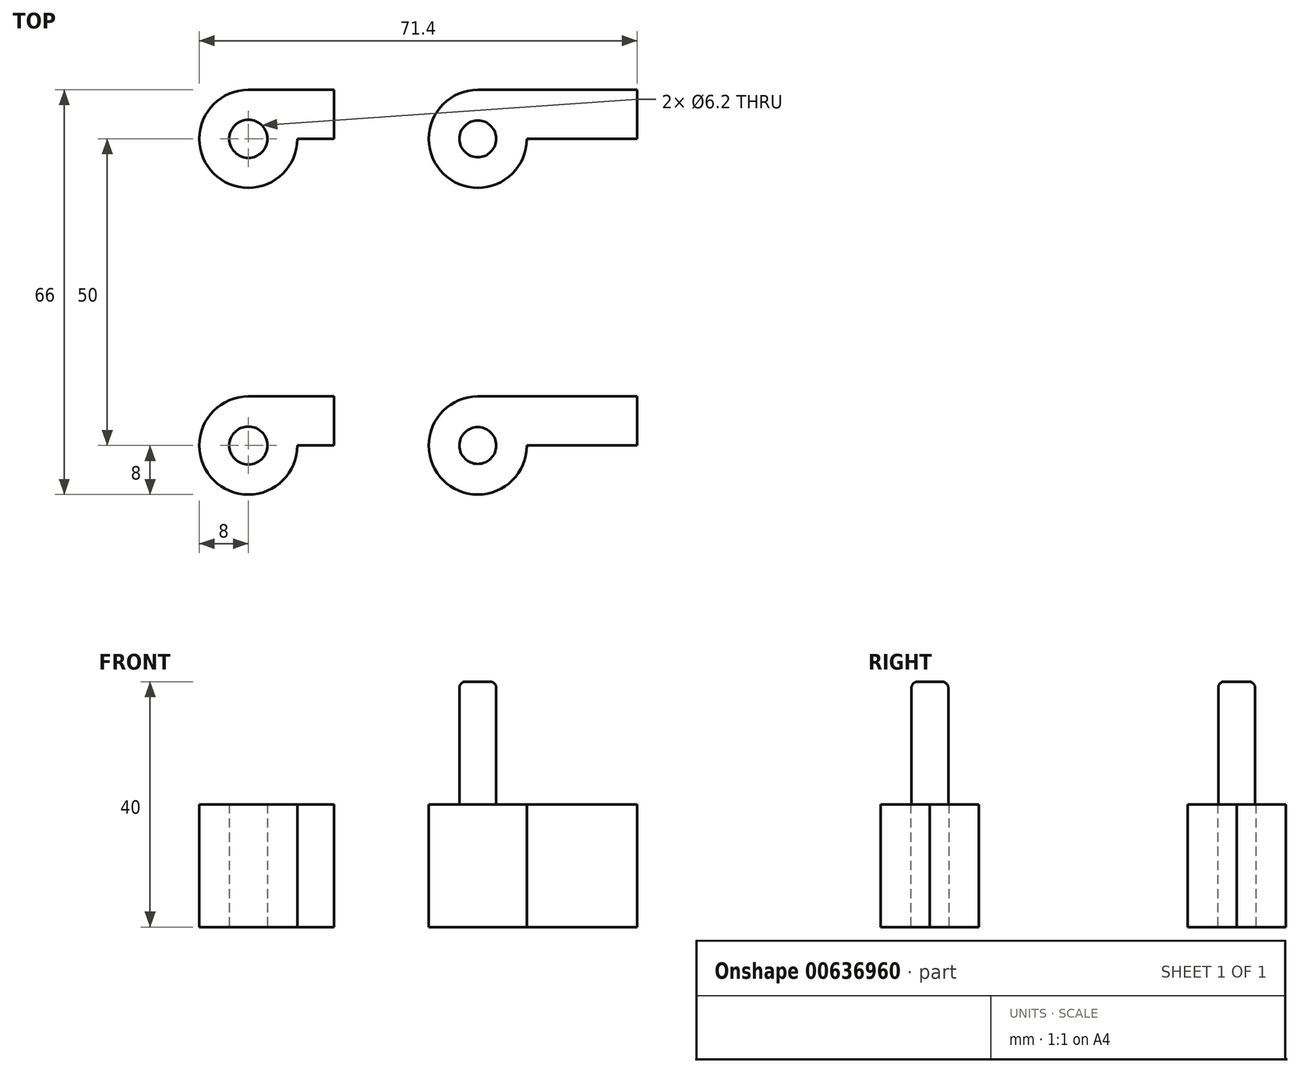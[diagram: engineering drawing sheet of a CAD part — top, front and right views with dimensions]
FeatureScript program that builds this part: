
annotation { "Feature Type Name" : "Feature", "Feature Type Description" : "" }
export const myFeature = defineFeature(function(context is Context, id is Id, definition is map)
    precondition{}
    {
        {
            var Q0;
            Q0=qCreatedBy(makeId("Top.planeOp"),FACE);
            var sketch = newSketch(context, id + "F0", { "sketchPlane" : qUnion([Q0])});
            skLineSegment(sketch, "E0.top", {"start": v(0, 8) * mm, "end": v(14, 8) * mm});
            skLineSegment(sketch, "E0.right", {"start": v(14, 0) * mm, "end": v(14, 8) * mm});
            skArc(sketch, "E1", {"start": v(0, 8) * mm, "mid": v(-5.66, -5.66) * mm, "end": v(8, 0) * mm});
            skCircle(sketch, "E2", {"center": v(0, 0) * mm, "radius": 3.1 * mm});
            skLineSegment(sketch, "E3.trimOffspring", {"start": v(8, 0) * mm, "end": v(14, 0) * mm});
            skSolve(sketch);
        }
        {
            var Q0;
            Q0=makeQuery(id+"F0.imprint","IMPRINT",FACE,{"disambiguationData":[TD([[makeQuery(id+"F0.imprint","IMPRINT",EDGE,{"derivedFrom":sQuery(id+"F0.wireOp",EDGE,"E0.top")}),-1.0]])]});
            extrude(context, id + "F1", {"entities" : qUnion([Q0]), "depth" : 20 * mm, "offsetDistance" : 25 * mm});
        }
        {
            var Q0;
            Q0=makeQuery(id+"F1.opExtrude","SWEPT_BODY",BODY,{"disambiguationData":[OSD([sQuery(id+"F0.wireOp",EDGE,"E0.top"),sQuery(id+"F0.wireOp",EDGE,"E0.right"),sQuery(id+"F0.wireOp",EDGE,"E1"),sQuery(id+"F0.wireOp",EDGE,"E2"),sQuery(id+"F0.wireOp",EDGE,"E3.trimOffspring")])]});
            transform(context, id + "F2", {"entities" : qUnion([Q0]), "transformType" : TransformType.TRANSLATION_3D, "dx" : 111.7 * mm, "dy" : 0 * mm, "dz" : 0 * mm, "makeCopy" : true});
        }
        {
            var Q0;
            Q0=makeQuery(id+"F2.opPattern","COPY",FACE,{"derivedFrom":makeQuery(id+"F1.opExtrude","SWEPT_FACE",FACE,{"disambiguationData":[OSD([sQuery(id+"F0.wireOp",EDGE,"E0.right")])]}),"instanceName":"1"});
            cPlane(context, id + "F3", {"entities" : qUnion([Q0]), "cplaneType" : CPlaneType.OFFSET, "offset" : 0 * mm, "width" : 150 * mm, "height" : 150 * mm});
        }
        {
            var Q0;
            Q0=qCreatedBy(id+"F3.planeOp",FACE);
            var sketch = newSketch(context, id + "F4", { "sketchPlane" : qUnion([Q0])});
            skLineSegment(sketch, "E4.0.0", {"start": v(0, 0) * mm, "end": v(8, 0) * mm});
            skLineSegment(sketch, "E4.0.1", {"start": v(8, 0) * mm, "end": v(8, 20) * mm});
            skLineSegment(sketch, "E4.0.2", {"start": v(8, 20) * mm, "end": v(0, 20) * mm});
            skLineSegment(sketch, "E4.0.3", {"start": v(0, 20) * mm, "end": v(0, 0) * mm});
            skSolve(sketch);
        }
        {
            var Q0;
            Q0=makeQuery(id+"F4.imprint","IMPRINT",FACE,{"disambiguationData":[TD([[makeQuery(id+"F4.imprint","IMPRINT",EDGE,{"derivedFrom":sQuery(id+"F4.wireOp",EDGE,"E4.0.0")}),1.0]])]});
            extrude(context, id + "F5", {"entities" : qUnion([Q0]), "operationType" : NewBodyOperationType.ADD, "depth" : 12 * mm, "offsetDistance" : 25 * mm});
        }
        {
            var Q0;
            Q0=makeQuery(id+"F5.boolean.opBoolean","MERGE",FACE,{"derivedFrom":[makeQuery(id+"F2.opPattern","COPY",FACE,{"derivedFrom":makeQuery(id+"F1.opExtrude","CAP_FACE",FACE,{"disambiguationData":[OSD([sQuery(id+"F0.wireOp",EDGE,"E0.top"),sQuery(id+"F0.wireOp",EDGE,"E0.right"),sQuery(id+"F0.wireOp",EDGE,"E1"),sQuery(id+"F0.wireOp",EDGE,"E2"),sQuery(id+"F0.wireOp",EDGE,"E3.trimOffspring")])],"isStart":false}),"instanceName":"1"}),makeQuery(id+"F5.opExtrude","SWEPT_FACE",FACE,{"disambiguationData":[OSD([sQuery(id+"F4.wireOp",EDGE,"E4.0.2")])]})]});
            cPlane(context, id + "F6", {"entities" : qUnion([Q0]), "cplaneType" : CPlaneType.OFFSET, "offset" : 0 * mm, "width" : 150 * mm, "height" : 150 * mm});
        }
        {
            var Q0;
            Q0=qCreatedBy(id+"F6.planeOp",FACE);
            var sketch = newSketch(context, id + "F7", { "sketchPlane" : qUnion([Q0])});
            skCircle(sketch, "E5.0", {"center": v(111.7, 0) * mm, "radius": 3.1 * mm});
            skSolve(sketch);
        }
        {
            var Q0;
            Q0=makeQuery(id+"F7.imprint","IMPRINT",FACE,{"disambiguationData":[TD([[makeQuery(id+"F7.imprint","IMPRINT",EDGE,{"derivedFrom":sQuery(id+"F7.wireOp",EDGE,"E5.0")}),1.0]])]});
            extrude(context, id + "F8", {"entities" : qUnion([Q0]), "operationType" : NewBodyOperationType.ADD, "oppositeDirection" : true, "depth" : 20 * mm, "offsetDistance" : 25 * mm});
        }
        {
            var Q0;
            Q0=qCreatedBy(id+"F6.planeOp",FACE);
            var sketch = newSketch(context, id + "F9", { "sketchPlane" : qUnion([Q0])});
            skArc(sketch, "E6.0.0", {"start": v(111.7, 8) * mm, "mid": v(106.04, -5.66) * mm, "end": v(119.7, 0) * mm});
            skLineSegment(sketch, "E6.0.1", {"start": v(119.7, 0) * mm, "end": v(137.7, 0) * mm});
            skLineSegment(sketch, "E6.0.2", {"start": v(137.7, 0) * mm, "end": v(137.7, 8) * mm});
            skLineSegment(sketch, "E6.0.3", {"start": v(137.7, 8) * mm, "end": v(111.7, 8) * mm});
            skCircle(sketch, "E7", {"center": v(111.7, 0) * mm, "radius": 3 * mm});
            skSolve(sketch);
        }
        {
            var Q0;
            Q0=makeQuery(id+"F9.imprint","IMPRINT",FACE,{"disambiguationData":[TD([[makeQuery(id+"F9.imprint","IMPRINT",EDGE,{"derivedFrom":sQuery(id+"F9.wireOp",EDGE,"E7")}),1.0]])]});
            extrude(context, id + "F10", {"entities" : qUnion([Q0]), "operationType" : NewBodyOperationType.ADD, "depth" : 20 * mm, "offsetDistance" : 25 * mm});
        }
        {
            var Q0;
            Q0=makeQuery(id+"F10.opExtrude","CAP_EDGE",EDGE,{"disambiguationData":[OSD([sQuery(id+"F9.wireOp",EDGE,"E7")])],"isStart":false});
            fillet(context, id + "F11", {"entities" : qUnion([Q0]), "radius" : 1 * mm, "tangentPropagation" : true, "allowEdgeOverflow" : false});
        }
        {
            var Q0;
            Q0=makeQuery(id+"F2.opPattern","COPY",BODY,{"derivedFrom":makeQuery(id+"F1.opExtrude","SWEPT_BODY",BODY,{"disambiguationData":[OSD([sQuery(id+"F0.wireOp",EDGE,"E0.top"),sQuery(id+"F0.wireOp",EDGE,"E0.right"),sQuery(id+"F0.wireOp",EDGE,"E1"),sQuery(id+"F0.wireOp",EDGE,"E2"),sQuery(id+"F0.wireOp",EDGE,"E3.trimOffspring")])]}),"instanceName":"1"});
            transform(context, id + "F12", {"entities" : qUnion([Q0]), "transformType" : TransformType.TRANSLATION_3D, "dx" : -74.3 * mm, "dy" : 0 * mm, "dz" : 0 * mm, "makeCopy" : false});
        }
        {
            var Q0;
            Q0=makeQuery(id+"F1.opExtrude","SWEPT_BODY",BODY,{"disambiguationData":[OSD([sQuery(id+"F0.wireOp",EDGE,"E0.top"),sQuery(id+"F0.wireOp",EDGE,"E0.right"),sQuery(id+"F0.wireOp",EDGE,"E1"),sQuery(id+"F0.wireOp",EDGE,"E2"),sQuery(id+"F0.wireOp",EDGE,"E3.trimOffspring")])]});
            transform(context, id + "F13", {"entities" : qUnion([Q0]), "transformType" : TransformType.TRANSLATION_3D, "dx" : 0 * mm, "dy" : 50 * mm, "dz" : 0 * mm, "makeCopy" : true});
        }
        {
            var Q0;
            Q0=makeQuery(id+"F2.opPattern","COPY",BODY,{"derivedFrom":makeQuery(id+"F1.opExtrude","SWEPT_BODY",BODY,{"disambiguationData":[OSD([sQuery(id+"F0.wireOp",EDGE,"E0.top"),sQuery(id+"F0.wireOp",EDGE,"E0.right"),sQuery(id+"F0.wireOp",EDGE,"E1"),sQuery(id+"F0.wireOp",EDGE,"E2"),sQuery(id+"F0.wireOp",EDGE,"E3.trimOffspring")])]}),"instanceName":"1"});
            transform(context, id + "F14", {"entities" : qUnion([Q0]), "transformType" : TransformType.TRANSLATION_3D, "dx" : 0 * mm, "dy" : 50 * mm, "dz" : 0 * mm, "makeCopy" : true});
        }
    });
